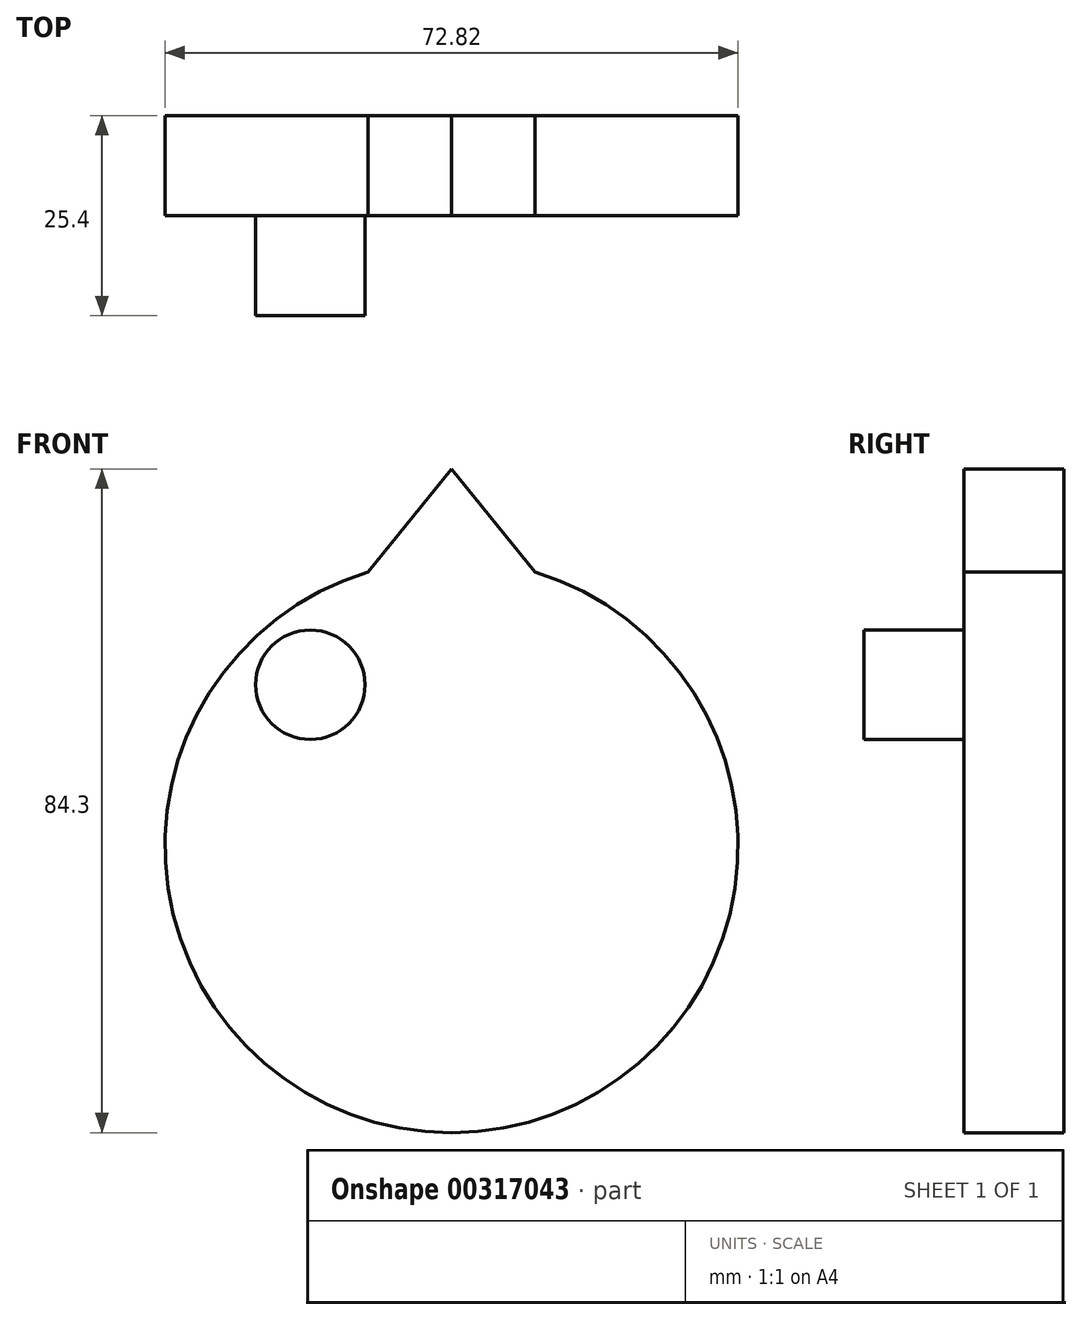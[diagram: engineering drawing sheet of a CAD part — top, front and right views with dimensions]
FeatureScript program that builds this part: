
annotation { "Feature Type Name" : "Feature", "Feature Type Description" : "" }
export const myFeature = defineFeature(function(context is Context, id is Id, definition is map)
    precondition{}
    {
        {
            var Q0;
            Q0=qCreatedBy(makeId("Front.planeOp"),FACE);
            var sketch = newSketch(context, id + "F0", { "sketchPlane" : qUnion([Q0])});
            skCircle(sketch, "E0", {"center": v(0, 0) * mm, "radius": 36.4 * mm});
            skSolve(sketch);
        }
        {
            var Q0;
            Q0 = qSketchRegion(id + "F0", true);
            extrude(context, id + "F1", {"entities" : qUnion([Q0]), "depth" : 12.7 * mm});
        }
        {
            var Q0;
            Q0=makeQuery(id+"F1.opExtrude","CAP_FACE",FACE,{"disambiguationData":[OSD([sQuery(id+"F0.wireOp",EDGE,"E0")])],"isStart":false});
            var sketch = newSketch(context, id + "F2", { "sketchPlane" : qUnion([Q0])});
            skCircle(sketch, "E1", {"center": v(-17.93, 20.5) * mm, "radius": 6.94 * mm});
            skSolve(sketch);
        }
        {
            var Q0;
            Q0 = qSketchRegion(id + "F2", true);
            extrude(context, id + "F3", {"entities" : qUnion([Q0]), "operationType" : NewBodyOperationType.ADD, "depth" : 12.7 * mm});
        }
        {
            var Q0;
            {var subQ0=sQuery(id+"F2.wireOp",EDGE,"E1");var subQ1=sQuery(id+"F0.wireOp",EDGE,"E0");Q0=makeQuery(id+"FYC5p4ih0OX00AX_1.23.F3.boolean.opBoolean","SPLIT",FACE,{"disambiguationData":[TD([makeQuery(id+"F1.opExtrude","SWEPT_FACE",FACE,{"disambiguationData":[OSD([subQ1])]}),makeQuery(id+"F3.opExtrude","SWEPT_FACE",FACE,{"disambiguationData":[OSD([subQ0])]}),makeQuery(id+"FYC5p4ih0OX00AX_1.1.F3.opExtrude","SWEPT_FACE",FACE,{"disambiguationData":[OSD([subQ0])]}),makeQuery(id+"FYC5p4ih0OX00AX_1.2.F3.opExtrude","SWEPT_FACE",FACE,{"disambiguationData":[OSD([subQ0])]}),makeQuery(id+"FYC5p4ih0OX00AX_1.3.F3.opExtrude","SWEPT_FACE",FACE,{"disambiguationData":[OSD([subQ0])]}),makeQuery(id+"FYC5p4ih0OX00AX_1.4.F3.opExtrude","SWEPT_FACE",FACE,{"disambiguationData":[OSD([subQ0])]}),makeQuery(id+"FYC5p4ih0OX00AX_1.5.F3.opExtrude","SWEPT_FACE",FACE,{"disambiguationData":[OSD([subQ0])]}),makeQuery(id+"FYC5p4ih0OX00AX_1.6.F3.opExtrude","SWEPT_FACE",FACE,{"disambiguationData":[OSD([subQ0])]}),makeQuery(id+"FYC5p4ih0OX00AX_1.7.F3.opExtrude","SWEPT_FACE",FACE,{"disambiguationData":[OSD([subQ0])]}),makeQuery(id+"FYC5p4ih0OX00AX_1.8.F3.opExtrude","SWEPT_FACE",FACE,{"disambiguationData":[OSD([subQ0])]}),makeQuery(id+"FYC5p4ih0OX00AX_1.9.F3.opExtrude","SWEPT_FACE",FACE,{"disambiguationData":[OSD([subQ0])]}),makeQuery(id+"FYC5p4ih0OX00AX_1.10.F3.opExtrude","SWEPT_FACE",FACE,{"disambiguationData":[OSD([subQ0])]}),makeQuery(id+"FYC5p4ih0OX00AX_1.11.F3.opExtrude","SWEPT_FACE",FACE,{"disambiguationData":[OSD([subQ0])]}),makeQuery(id+"FYC5p4ih0OX00AX_1.12.F3.opExtrude","SWEPT_FACE",FACE,{"disambiguationData":[OSD([subQ0])]}),makeQuery(id+"FYC5p4ih0OX00AX_1.13.F3.opExtrude","SWEPT_FACE",FACE,{"disambiguationData":[OSD([subQ0])]}),makeQuery(id+"FYC5p4ih0OX00AX_1.14.F3.opExtrude","SWEPT_FACE",FACE,{"disambiguationData":[OSD([subQ0])]}),makeQuery(id+"FYC5p4ih0OX00AX_1.15.F3.opExtrude","SWEPT_FACE",FACE,{"disambiguationData":[OSD([subQ0])]}),makeQuery(id+"FYC5p4ih0OX00AX_1.16.F3.opExtrude","SWEPT_FACE",FACE,{"disambiguationData":[OSD([subQ0])]}),makeQuery(id+"FYC5p4ih0OX00AX_1.17.F3.opExtrude","SWEPT_FACE",FACE,{"disambiguationData":[OSD([subQ0])]}),makeQuery(id+"FYC5p4ih0OX00AX_1.18.F3.opExtrude","SWEPT_FACE",FACE,{"disambiguationData":[OSD([subQ0])]}),makeQuery(id+"FYC5p4ih0OX00AX_1.19.F3.opExtrude","SWEPT_FACE",FACE,{"disambiguationData":[OSD([subQ0])]}),makeQuery(id+"FYC5p4ih0OX00AX_1.20.F3.opExtrude","SWEPT_FACE",FACE,{"disambiguationData":[OSD([subQ0])]}),makeQuery(id+"FYC5p4ih0OX00AX_1.21.F3.opExtrude","SWEPT_FACE",FACE,{"disambiguationData":[OSD([subQ0])]}),makeQuery(id+"FYC5p4ih0OX00AX_1.22.F3.opExtrude","SWEPT_FACE",FACE,{"disambiguationData":[OSD([subQ0])]}),makeQuery(id+"FYC5p4ih0OX00AX_1.23.F3.opExtrude","SWEPT_FACE",FACE,{"disambiguationData":[OSD([subQ0])]})])],"derivedFrom":makeQuery(id+"F1.opExtrude","CAP_FACE",FACE,{"disambiguationData":[OSD([subQ1])],"isStart":false})});}
            var sketch = newSketch(context, id + "F4", { "sketchPlane" : qUnion([Q0])});
            skLineSegment(sketch, "E2", {"start": v(-10.63, 34.82) * mm, "end": v(0, 47.89) * mm});
            skLineSegment(sketch, "E3", {"start": v(0, 47.89) * mm, "end": v(10.63, 34.82) * mm});
            skArc(sketch, "E4.0", {"start": v(10.63, 34.82) * mm, "mid": v(-29.26, -21.66) * mm, "end": v(36.4, 0) * mm});
            skArc(sketch, "E5.0", {"start": v(36.4, 0) * mm, "mid": v(21.66, 29.26) * mm, "end": v(-10.63, 34.82) * mm});
            skSolve(sketch);
        }
        {
            var Q0;
            {var subQ0=sQuery(id+"F4.wireOp",EDGE,"E2");Q0=makeQuery(id+"F4.imprint","IMPRINT",FACE,{"disambiguationData":[TD([[makeQuery(id+"F4.imprint","IMPRINT",EDGE,{"derivedFrom":subQ0}),-1.0]])]});}
            extrude(context, id + "F5", {"entities" : qUnion([Q0]), "operationType" : NewBodyOperationType.ADD, "oppositeDirection" : true, "depth" : 12.7 * mm});
        }
    });
